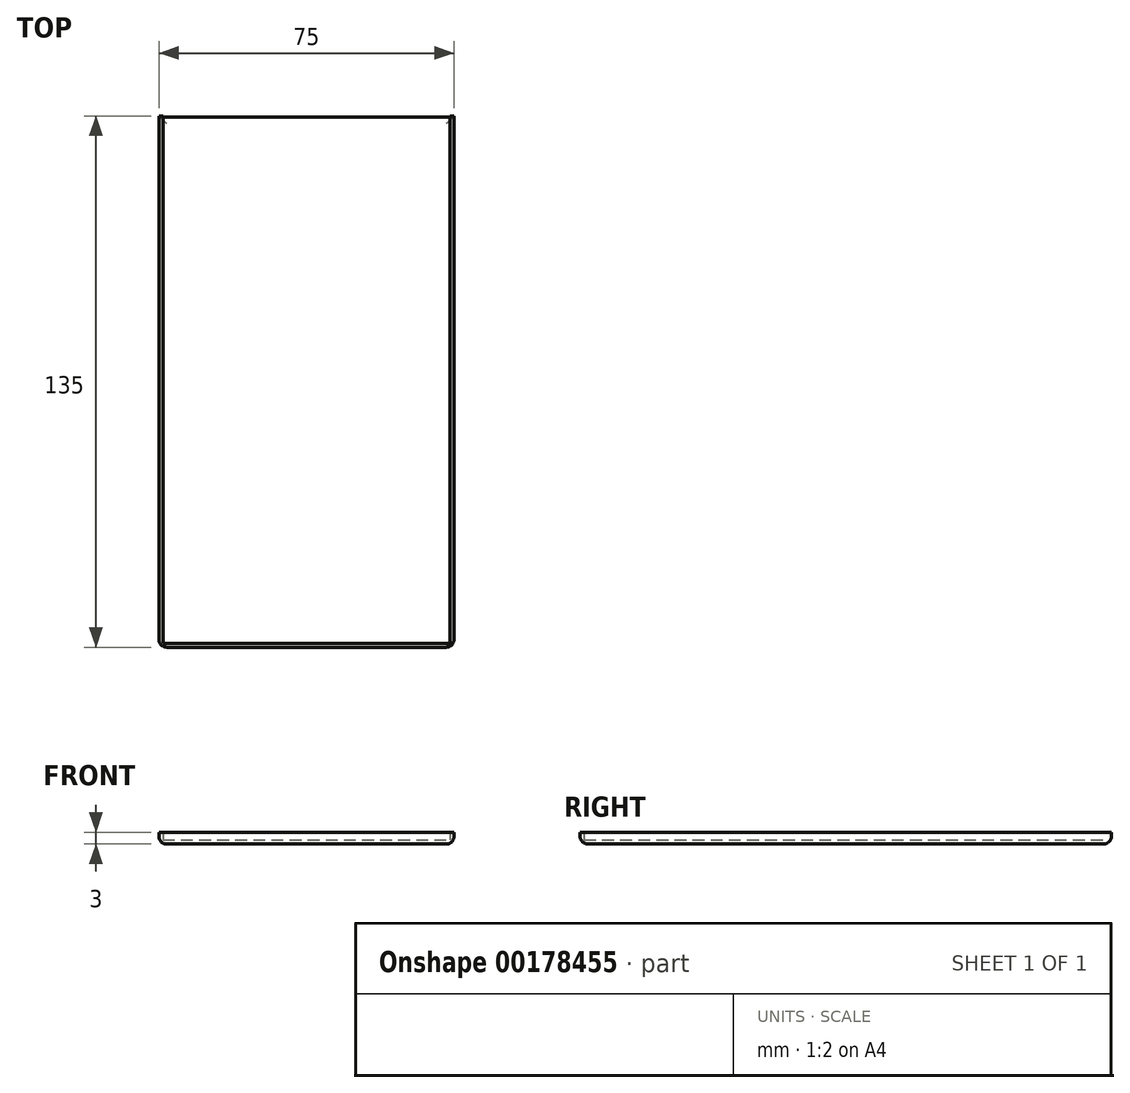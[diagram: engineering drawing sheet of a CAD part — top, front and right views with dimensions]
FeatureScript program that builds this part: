
annotation { "Feature Type Name" : "Feature", "Feature Type Description" : "" }
export const myFeature = defineFeature(function(context is Context, id is Id, definition is map)
    precondition{}
    {
        {
            var Q0;
            Q0=qCreatedBy(makeId("Top.planeOp"),FACE);
            var sketch = newSketch(context, id + "F0", { "sketchPlane" : qUnion([Q0])});
            skLineSegment(sketch, "E0.bottom", {"start": v(0, 0) * mm, "end": v(75, 0) * mm});
            skLineSegment(sketch, "E0.top", {"start": v(0, 135) * mm, "end": v(75, 135) * mm});
            skLineSegment(sketch, "E0.left", {"start": v(0, 0) * mm, "end": v(0, 135) * mm});
            skLineSegment(sketch, "E0.right", {"start": v(75, 0) * mm, "end": v(75, 135) * mm});
            skLineSegment(sketch, "E1.0", {"start": v(74, 1) * mm, "end": v(74, 135) * mm});
            skLineSegment(sketch, "E1.1", {"start": v(1, 1) * mm, "end": v(74, 1) * mm});
            skLineSegment(sketch, "E1.2", {"start": v(1, 1) * mm, "end": v(1, 135) * mm});
            skSolve(sketch);
        }
        {
            var Q0;
            Q0=makeQuery(id+"F0.imprint","IMPRINT",FACE,{"disambiguationData":[TD([[makeQuery(id+"F0.imprint","IMPRINT",EDGE,{"derivedFrom":sQuery(id+"F0.wireOp",EDGE,"E0.bottom")}),1.0]])]});
            extrude(context, id + "F1", {"entities" : qUnion([Q0]), "depth" : 3 * mm});
        }
        {
            var Q0;
            {var subQ0=sQuery(id+"F0.wireOp",EDGE,"E1.0");Q0=makeQuery(id+"F0.imprint","IMPRINT",FACE,{"disambiguationData":[TD([[makeQuery(id+"F0.imprint","IMPRINT",EDGE,{"derivedFrom":subQ0}),1.0]])]});}
            extrude(context, id + "F2", {"entities" : qUnion([Q0]), "operationType" : NewBodyOperationType.ADD, "depth" : 1 * mm});
        }
        {
            var Q0;
            {var subQ0=sQuery(id+"F0.wireOp",EDGE,"E1.2");var subQ1=sQuery(id+"F0.wireOp",EDGE,"E1.1");var subQ2=sQuery(id+"F0.wireOp",EDGE,"E1.0");var subQ3=sQuery(id+"F0.wireOp",EDGE,"E0.top");Q0=makeQuery(id+"F2.boolean.opBoolean","MERGE",FACE,{"derivedFrom":[makeQuery(id+"F1.opExtrude","CAP_FACE",FACE,{"disambiguationData":[OSD([sQuery(id+"F0.wireOp",EDGE,"E0.bottom"),subQ3,sQuery(id+"F0.wireOp",EDGE,"E0.left"),sQuery(id+"F0.wireOp",EDGE,"E0.right"),subQ2,subQ1,subQ0])],"isStart":true}),makeQuery(id+"F2.opExtrude","CAP_FACE",FACE,{"disambiguationData":[OSD([subQ3,subQ2,subQ1,subQ0])],"isStart":true})]});}
            fillet(context, id + "F3", {"entities" : qUnion([Q0]), "radius" : 2 * mm, "tangentPropagation" : true, "allowEdgeOverflow" : false});
        }
        {
            var Q0;
            Q0=makeQuery(id+"F1.opExtrude","SWEPT_EDGE",EDGE,{"disambiguationData":[OSD([sQuery(id+"F0.wireOp",EDGE,"E0.bottom"),sQuery(id+"F0.wireOp",EDGE,"E0.right")])]});
            var Q1;
            Q1=makeQuery(id+"F1.opExtrude","SWEPT_EDGE",EDGE,{"disambiguationData":[OSD([sQuery(id+"F0.wireOp",EDGE,"E0.bottom"),sQuery(id+"F0.wireOp",EDGE,"E0.left")])]});
            fillet(context, id + "F4", {"entities" : qUnion([Q0, Q1]), "radius" : 2 * mm, "tangentPropagation" : true, "allowEdgeOverflow" : false});
        }
    });
